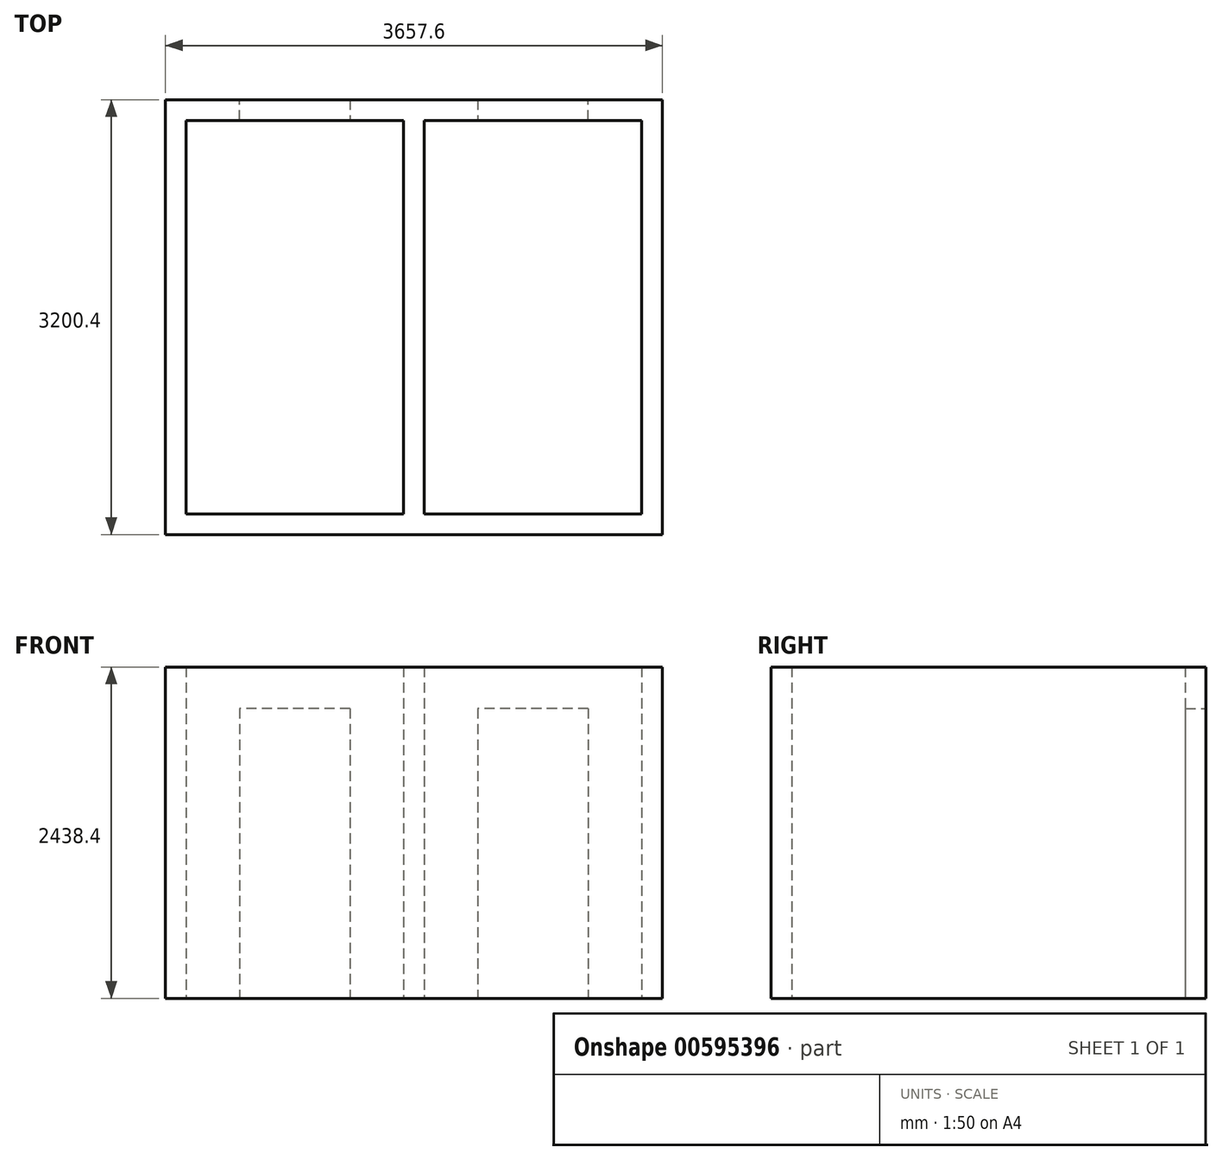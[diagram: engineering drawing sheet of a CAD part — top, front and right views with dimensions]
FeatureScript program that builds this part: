
annotation { "Feature Type Name" : "Feature", "Feature Type Description" : "" }
export const myFeature = defineFeature(function(context is Context, id is Id, definition is map)
    precondition{}
    {
        {
            var Q0;
            Q0=qCreatedBy(makeId("Top.planeOp"),FACE);
            var sketch = newSketch(context, id + "F0", { "sketchPlane" : qUnion([Q0])});
            skLineSegment(sketch, "E0", {"start": v(3352.8, 0) * mm, "end": v(3352.8, 2895.6) * mm});
            skLineSegment(sketch, "E1", {"start": v(3352.8, 2895.6) * mm, "end": v(0, 2895.6) * mm});
            skLineSegment(sketch, "E2", {"start": v(0, 2895.6) * mm, "end": v(0, 0) * mm});
            skLineSegment(sketch, "E3.0", {"start": v(-152.4, 2895.6) * mm, "end": v(-152.4, 0) * mm});
            skLineSegment(sketch, "E4.0", {"start": v(3352.8, 3048) * mm, "end": v(0, 3048) * mm});
            skLineSegment(sketch, "E5.0", {"start": v(3505.2, 0) * mm, "end": v(3505.2, 2895.6) * mm});
            skLineSegment(sketch, "E6.0", {"start": v(0, -152.4) * mm, "end": v(3352.8, -152.4) * mm});
            skLineSegment(sketch, "E7.0", {"start": v(-157.13, 2895.6) * mm, "end": v(-157.13, 0) * mm});
            skLineSegment(sketch, "E8", {"start": v(-152.4, 2895.6) * mm, "end": v(-152.4, 3048) * mm});
            skLineSegment(sketch, "E9", {"start": v(-152.4, 3048) * mm, "end": v(0, 3048) * mm});
            skLineSegment(sketch, "E10", {"start": v(3352.8, 3048) * mm, "end": v(3505.2, 3048) * mm});
            skLineSegment(sketch, "E11", {"start": v(3505.2, 3048) * mm, "end": v(3505.2, 2895.6) * mm});
            skLineSegment(sketch, "E12", {"start": v(3352.8, -152.4) * mm, "end": v(3505.2, -152.4) * mm});
            skLineSegment(sketch, "E13", {"start": v(3505.2, -152.4) * mm, "end": v(3505.2, 0) * mm});
            skLineSegment(sketch, "E14", {"start": v(-152.4, 0) * mm, "end": v(-152.4, -152.4) * mm});
            skLineSegment(sketch, "E15", {"start": v(-152.4, -152.4) * mm, "end": v(0, -152.4) * mm});
            skLineSegment(sketch, "E16.0", {"start": v(1600.2, 2895.6) * mm, "end": v(1600.2, 0) * mm});
            skLineSegment(sketch, "E17.0", {"start": v(1752.6, 2895.6) * mm, "end": v(1752.6, 0) * mm});
            skLineSegment(sketch, "E18", {"start": v(0, 0) * mm, "end": v(3352.8, 0) * mm});
            skLineSegment(sketch, "E19", {"start": v(0, 2895.6) * mm, "end": v(393.7, 2895.6) * mm});
            skLineSegment(sketch, "E20", {"start": v(393.7, 2895.6) * mm, "end": v(393.7, 3048) * mm});
            skLineSegment(sketch, "E21", {"start": v(393.7, 3048) * mm, "end": v(1206.5, 3048) * mm});
            skLineSegment(sketch, "E22", {"start": v(1206.5, 3048) * mm, "end": v(1206.5, 2895.6) * mm});
            skLineSegment(sketch, "E23", {"start": v(1206.5, 2895.6) * mm, "end": v(393.7, 2895.6) * mm});
            skLineSegment(sketch, "E24", {"start": v(3352.8, 2895.6) * mm, "end": v(2959.1, 2895.6) * mm});
            skLineSegment(sketch, "E25", {"start": v(2959.1, 2895.6) * mm, "end": v(2959.1, 3048) * mm});
            skLineSegment(sketch, "E26", {"start": v(2959.1, 3048) * mm, "end": v(2146.3, 3048) * mm});
            skLineSegment(sketch, "E27", {"start": v(2146.3, 3048) * mm, "end": v(2146.3, 2895.6) * mm});
            skLineSegment(sketch, "E28", {"start": v(2146.3, 2895.6) * mm, "end": v(2959.1, 2895.6) * mm});
            skSolve(sketch);
        }
        {
            var Q0;
            {var subQ1=sQuery(id+"F0.wireOp",EDGE,"E0");Q0=makeQuery(id+"F0.imprint","IMPRINT",FACE,{"disambiguationData":[TD([[makeQuery(id+"F0.imprint","IMPRINT",EDGE,{"derivedFrom":subQ1}),-1.0]])]});}
            var Q1;
            {var subQ0=sQuery(id+"F0.wireOp",EDGE,"E16.0");Q1=makeQuery(id+"F0.imprint","IMPRINT",FACE,{"disambiguationData":[TD([[makeQuery(id+"F0.imprint","IMPRINT",EDGE,{"derivedFrom":subQ0}),1.0]])]});}
            var Q2;
            Q2=makeQuery(id+"F0.imprint","IMPRINT",FACE,{"disambiguationData":[TD([[makeQuery(id+"F0.imprint","IMPRINT",EDGE,{"derivedFrom":sQuery(id+"F0.wireOp",EDGE,"E20")}),-1.0]])]});
            extrude(context, id + "F1", {"entities" : qUnion([Q0, Q1, Q2]), "depth" : 2438.4 * mm, "offsetDistance" : 25.4 * mm});
        }
        {
            var Q0;
            Q0=makeQuery(id+"F0.imprint","IMPRINT",FACE,{"disambiguationData":[TD([[makeQuery(id+"F0.imprint","IMPRINT",EDGE,{"derivedFrom":sQuery(id+"F0.wireOp",EDGE,"E20")}),-1.0]])]});
            extrude(context, id + "F2", {"entities" : qUnion([Q0]), "operationType" : NewBodyOperationType.REMOVE, "depth" : 2133.6 * mm, "offsetDistance" : 25.4 * mm});
        }
        {
            var Q0;
            {var subQ0=sQuery(id+"F0.wireOp",EDGE,"E22");Q0=makeQuery(id+"F0.imprint","IMPRINT",FACE,{"disambiguationData":[TD([[makeQuery(id+"F0.imprint","IMPRINT",EDGE,{"derivedFrom":subQ0}),1.0]])]});}
            extrude(context, id + "F3", {"entities" : qUnion([Q0]), "operationType" : NewBodyOperationType.ADD, "depth" : 2438.4 * mm, "offsetDistance" : 25.4 * mm});
        }
        {
            var Q0;
            Q0=makeQuery(id+"F0.imprint","IMPRINT",FACE,{"disambiguationData":[TD([[makeQuery(id+"F0.imprint","IMPRINT",EDGE,{"derivedFrom":sQuery(id+"F0.wireOp",EDGE,"E25")}),1.0]])]});
            extrude(context, id + "F4", {"entities" : qUnion([Q0]), "operationType" : NewBodyOperationType.ADD, "depth" : 2438.4 * mm, "offsetDistance" : 25.4 * mm});
        }
        {
            var Q0;
            Q0=makeQuery(id+"F0.imprint","IMPRINT",FACE,{"disambiguationData":[TD([[makeQuery(id+"F0.imprint","IMPRINT",EDGE,{"derivedFrom":sQuery(id+"F0.wireOp",EDGE,"E25")}),1.0]])]});
            extrude(context, id + "F5", {"entities" : qUnion([Q0]), "operationType" : NewBodyOperationType.REMOVE, "depth" : 2133.6 * mm, "offsetDistance" : 25.4 * mm});
        }
    });
